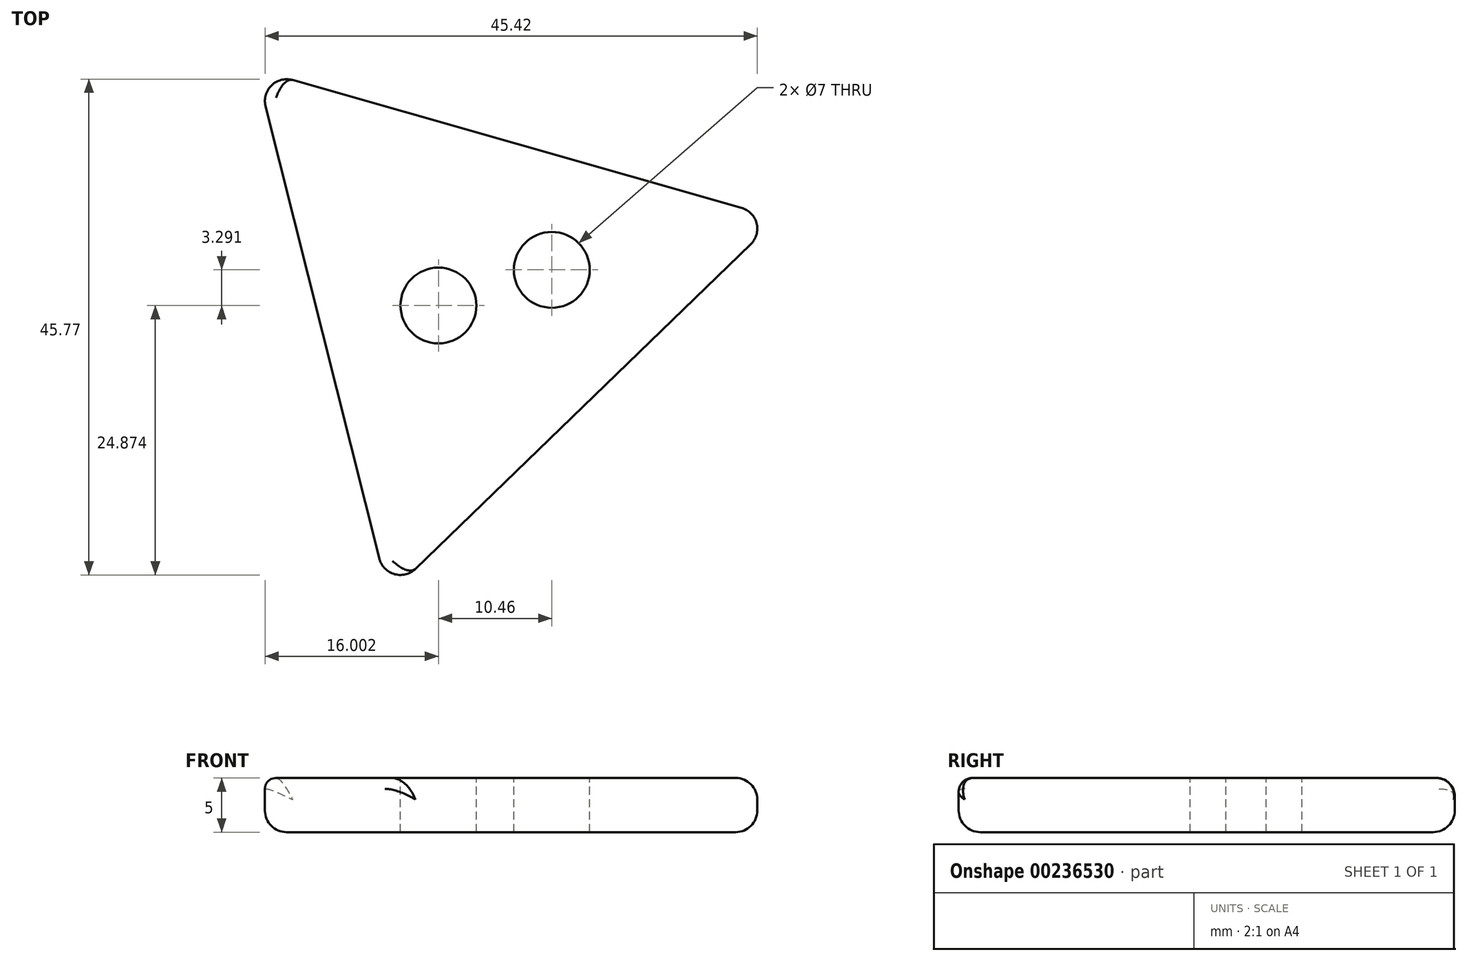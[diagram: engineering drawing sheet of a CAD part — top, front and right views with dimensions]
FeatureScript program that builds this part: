
annotation { "Feature Type Name" : "Feature", "Feature Type Description" : "" }
export const myFeature = defineFeature(function(context is Context, id is Id, definition is map)
    precondition{}
    {
        {
            var Q0;
            Q0=qCreatedBy(makeId("Top.planeOp"),FACE);
            var sketch = newSketch(context, id + "F0", { "sketchPlane" : qUnion([Q0])});
            skCircle(sketch, "E0.cCircle", {"center": v(-14.24, 13.94) * mm, "radius": 14.43 * mm, "construction": true});
            skLineSegment(sketch, "E0.0", {"start": v(13.76, 20.98) * mm, "end": v(-22.15, -13.82) * mm});
            skLineSegment(sketch, "E0.1", {"start": v(-22.15, -13.82) * mm, "end": v(-34.33, 34.67) * mm});
            skLineSegment(sketch, "E0.2", {"start": v(-34.33, 34.67) * mm, "end": v(13.76, 20.98) * mm});
            skPoint(sketch, "E0.0.midPoint", {"position": v(-4.2, 3.58) * mm});
            skSolve(sketch);
        }
        {
            var Q0;
            Q0 = qSketchRegion(id + "F0", true);
            extrude(context, id + "F1", {"entities" : qUnion([Q0]), "depth" : 5 * mm});
        }
        {
            var Q0;
            Q0=makeQuery(id+"F1.opExtrude","CAP_EDGE",EDGE,{"disambiguationData":[OSD([sQuery(id+"F0.wireOp",EDGE,"E0.1")])],"isStart":false});
            fillet(context, id + "F2", {"entities" : qUnion([Q0]), "radius" : 1 * mm, "tangentPropagation" : true, "allowEdgeOverflow" : false});
        }
        {
            var Q0;
            Q0=makeQuery(id+"F1.opExtrude","CAP_EDGE",EDGE,{"disambiguationData":[OSD([sQuery(id+"F0.wireOp",EDGE,"E0.2")])],"isStart":false});
            var Q1;
            Q1=makeQuery(id+"F1.opExtrude","CAP_EDGE",EDGE,{"disambiguationData":[OSD([sQuery(id+"F0.wireOp",EDGE,"E0.0")])],"isStart":false});
            var Q2;
            Q2=makeQuery(id+"F1.opExtrude","CAP_EDGE",EDGE,{"disambiguationData":[OSD([sQuery(id+"F0.wireOp",EDGE,"E0.0")])],"isStart":true});
            var Q3;
            Q3=makeQuery(id+"F1.opExtrude","CAP_EDGE",EDGE,{"disambiguationData":[OSD([sQuery(id+"F0.wireOp",EDGE,"E0.1")])],"isStart":true});
            var Q4;
            Q4=makeQuery(id+"F1.opExtrude","CAP_EDGE",EDGE,{"disambiguationData":[OSD([sQuery(id+"F0.wireOp",EDGE,"E0.2")])],"isStart":true});
            fillet(context, id + "F3", {"entities" : qUnion([Q0, Q1, Q2, Q3, Q4]), "radius" : 2 * mm, "tangentPropagation" : true, "allowEdgeOverflow" : false});
        }
        {
            var Q0;
            Q0=makeQuery(id+"F3.opFillet","BLEND_EDGE",EDGE,{"blendedFrom":[makeQuery(id+"F1.opExtrude","CAP_EDGE",EDGE,{"disambiguationData":[OSD([sQuery(id+"F0.wireOp",EDGE,"E0.0")])],"isStart":true}),makeQuery(id+"F1.opExtrude","CAP_EDGE",EDGE,{"disambiguationData":[OSD([sQuery(id+"F0.wireOp",EDGE,"E0.2")])],"isStart":true})],"blendedInto":[]});
            fillet(context, id + "F4", {"entities" : qUnion([Q0]), "radius" : 2 * mm, "tangentPropagation" : true, "allowEdgeOverflow" : false});
        }
        {
            var Q0;
            Q0=makeQuery(id+"F1.opExtrude","CAP_FACE",FACE,{"disambiguationData":[OSD([sQuery(id+"F0.wireOp",EDGE,"E0.0"),sQuery(id+"F0.wireOp",EDGE,"E0.1"),sQuery(id+"F0.wireOp",EDGE,"E0.2")])],"isStart":false});
            var sketch = newSketch(context, id + "F5", { "sketchPlane" : qUnion([Q0])});
            skPoint(sketch, "E1", {"position": v(-7.08, 16.2) * mm});
            skPoint(sketch, "E2", {"position": v(-17.54, 12.9) * mm});
            skSolve(sketch);
        }
        {
            var Q0;
            Q0=sQuery(id+"F5.wireOp",VERTEX,"E1");
            var Q1;
            Q1=sQuery(id+"F5.wireOp",VERTEX,"E2");
            var Q2;
            Q2=makeQuery(id+"F1.opExtrude","SWEPT_BODY",BODY,{"disambiguationData":[OSD([sQuery(id+"F0.wireOp",EDGE,"E0.0"),sQuery(id+"F0.wireOp",EDGE,"E0.1"),sQuery(id+"F0.wireOp",EDGE,"E0.2")])]});
            hole(context, id + "F6", {"style" : HoleStyle.SIMPLE, "endStyle" : HoleEndStyle.THROUGH, "holeDiameter" : 7 * mm, "locations" : qUnion([Q0, Q1]), "scope" : qUnion([Q2]), "isTappedThrough" : true});
        }
    });
